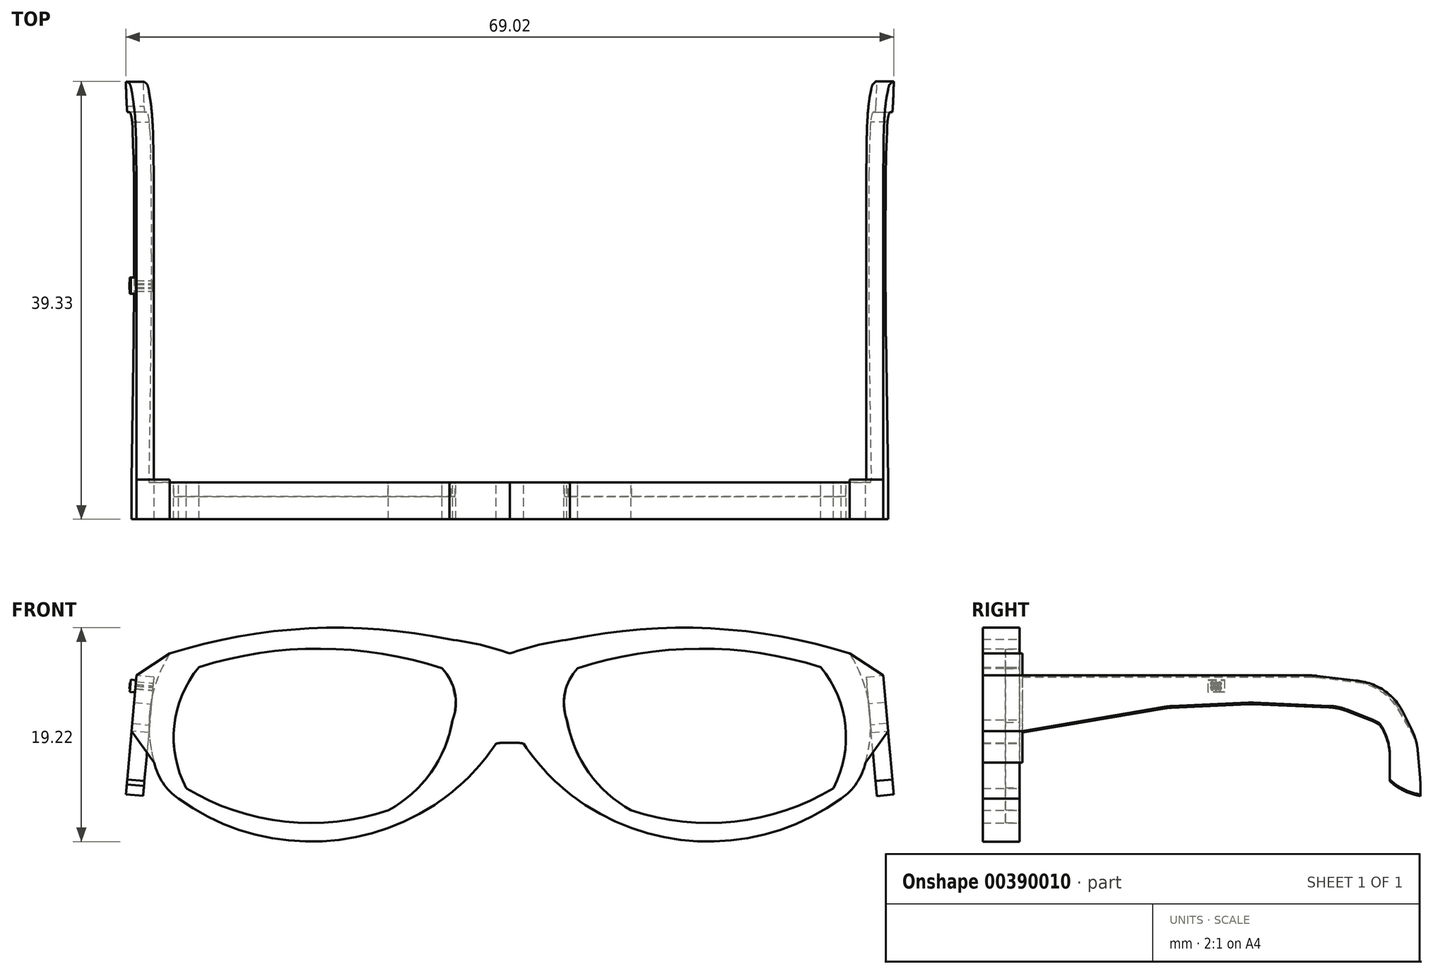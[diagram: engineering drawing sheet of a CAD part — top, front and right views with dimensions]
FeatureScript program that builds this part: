
annotation { "Feature Type Name" : "Feature", "Feature Type Description" : "" }
export const myFeature = defineFeature(function(context is Context, id is Id, definition is map)
    precondition{}
    {
        {
            var Q0;
            Q0=qCreatedBy(makeId("Front.planeOp"),FACE);
            var sketch = newSketch(context, id + "F0", { "sketchPlane" : qUnion([Q0])});
            skArc(sketch, "E0", {"start": v(27.94, 3.25) * mm, "mid": v(17.02, 4.8) * mm, "end": v(6.1, 3.16) * mm});
            skArc(sketch, "E1", {"start": v(29.08, -7.57) * mm, "mid": v(30, -2) * mm, "end": v(27.94, 3.25) * mm});
            skArc(sketch, "E2", {"start": v(10.95, -9.56) * mm, "mid": v(20.23, -10.57) * mm, "end": v(29.08, -7.57) * mm});
            skArc(sketch, "E3", {"start": v(5.25, -1.68) * mm, "mid": v(7.2, -6.28) * mm, "end": v(10.95, -9.56) * mm});
            skArc(sketch, "E4", {"start": v(6.1, 3.16) * mm, "mid": v(5.03, 0.85) * mm, "end": v(5.25, -1.68) * mm});
            skArc(sketch, "E5.MirrorCS", {"start": v(-27.94, 3.25) * mm, "mid": v(-17.02, 4.8) * mm, "end": v(-6.1, 3.16) * mm});
            skArc(sketch, "E6.MirrorCS", {"start": v(-6.1, 3.16) * mm, "mid": v(-5.03, 0.85) * mm, "end": v(-5.25, -1.68) * mm});
            skArc(sketch, "E7.MirrorCS", {"start": v(-5.25, -1.68) * mm, "mid": v(-7.2, -6.28) * mm, "end": v(-10.95, -9.56) * mm});
            skArc(sketch, "E8.MirrorCS", {"start": v(-10.95, -9.56) * mm, "mid": v(-20.23, -10.57) * mm, "end": v(-29.08, -7.57) * mm});
            skArc(sketch, "E9.MirrorCS", {"start": v(-29.08, -7.57) * mm, "mid": v(-30, -2) * mm, "end": v(-27.94, 3.25) * mm});
            skArc(sketch, "E10", {"start": v(10.95, -9.61) * mm, "mid": v(20.25, -10.67) * mm, "end": v(29.1, -7.6) * mm});
            skArc(sketch, "E11", {"start": v(5.15, -1.68) * mm, "mid": v(7.13, -6.32) * mm, "end": v(10.95, -9.61) * mm});
            skArc(sketch, "E12", {"start": v(6.1, 3.16) * mm, "mid": v(5, 0.85) * mm, "end": v(5.25, -1.68) * mm});
            skArc(sketch, "E13", {"start": v(27.94, 3.27) * mm, "mid": v(17, 4.88) * mm, "end": v(6.1, 3.16) * mm});
            skArc(sketch, "E14", {"start": v(29.08, -7.57) * mm, "mid": v(30.13, -1.98) * mm, "end": v(27.94, 3.27) * mm});
            skArc(sketch, "E15.MirrorCS", {"start": v(-5.15, -1.68) * mm, "mid": v(-7.13, -6.32) * mm, "end": v(-10.95, -9.61) * mm});
            skArc(sketch, "E16.MirrorCS", {"start": v(-10.95, -9.61) * mm, "mid": v(-20.25, -10.67) * mm, "end": v(-29.1, -7.6) * mm});
            skArc(sketch, "E17.MirrorCS", {"start": v(-29.08, -7.57) * mm, "mid": v(-30.13, -1.98) * mm, "end": v(-27.94, 3.27) * mm});
            skArc(sketch, "E18.MirrorCS", {"start": v(-27.94, 3.27) * mm, "mid": v(-17, 4.88) * mm, "end": v(-6.1, 3.16) * mm});
            skArc(sketch, "E19.MirrorCS", {"start": v(-6.1, 3.16) * mm, "mid": v(-5, 0.85) * mm, "end": v(-5.25, -1.68) * mm});
            skSolve(sketch);
        }
        {
            var Q0;
            Q0 = qSketchRegion(id + "F0", true);
            extrude(context, id + "F1", {"entities" : qUnion([Q0]), "depth" : 1.27 * mm});
        }
        {
            var Q0;
            Q0=qCreatedBy(makeId("Front.planeOp"),FACE);
            var sketch = newSketch(context, id + "F2", { "sketchPlane" : qUnion([Q0])});
            skArc(sketch, "E20", {"start": v(-6.09, 3.17) * mm, "mid": v(-17, 4.94) * mm, "end": v(-27.95, 3.27) * mm});
            skArc(sketch, "E21", {"start": v(-27.95, 3.27) * mm, "mid": v(-30.16, -2) * mm, "end": v(-29.08, -7.6) * mm});
            skArc(sketch, "E22", {"start": v(-29.08, -7.6) * mm, "mid": v(-20.21, -10.61) * mm, "end": v(-10.9, -9.6) * mm});
            skArc(sketch, "E23", {"start": v(-10.9, -9.6) * mm, "mid": v(-7.09, -6.19) * mm, "end": v(-5.13, -1.46) * mm});
            skArc(sketch, "E24", {"start": v(-5.13, -1.46) * mm, "mid": v(-4.95, 1) * mm, "end": v(-6.09, 3.17) * mm});
            skArc(sketch, "E25.MirrorCS", {"start": v(6.09, 3.17) * mm, "mid": v(17, 4.94) * mm, "end": v(27.95, 3.27) * mm});
            skArc(sketch, "E26.MirrorCS", {"start": v(5.13, -1.46) * mm, "mid": v(4.95, 1) * mm, "end": v(6.09, 3.17) * mm});
            skArc(sketch, "E27.MirrorCS", {"start": v(10.9, -9.6) * mm, "mid": v(7.09, -6.19) * mm, "end": v(5.13, -1.46) * mm});
            skArc(sketch, "E28.MirrorCS", {"start": v(29.08, -7.6) * mm, "mid": v(20.21, -10.61) * mm, "end": v(10.9, -9.6) * mm});
            skArc(sketch, "E29.MirrorCS", {"start": v(27.95, 3.27) * mm, "mid": v(30.16, -2) * mm, "end": v(29.08, -7.6) * mm});
            skSolve(sketch);
        }
        {
            var Q0;
            Q0=qCreatedBy(makeId("Front.planeOp"),FACE);
            var sketch = newSketch(context, id + "F3", { "sketchPlane" : qUnion([Q0])});
            skArc(sketch, "E30", {"start": v(0, -3.53) * mm, "mid": v(-0.62, -3.52) * mm, "end": v(-1.23, -3.59) * mm});
            skArc(sketch, "E31", {"start": v(-6.77, -9.12) * mm, "mid": v(-3.72, -6.63) * mm, "end": v(-1.23, -3.59) * mm});
            skArc(sketch, "E32", {"start": v(-29.78, -8.54) * mm, "mid": v(-18.37, -12.4) * mm, "end": v(-6.77, -9.12) * mm});
            skArc(sketch, "E33", {"start": v(-31.97, -5.28) * mm, "mid": v(-31.19, -7.12) * mm, "end": v(-29.78, -8.54) * mm});
            skArc(sketch, "E34", {"start": v(-30.56, 4.5) * mm, "mid": v(-32.3, -0.24) * mm, "end": v(-31.97, -5.28) * mm});
            skArc(sketch, "E35", {"start": v(-5.41, 5.77) * mm, "mid": v(-18.07, 6.76) * mm, "end": v(-30.56, 4.5) * mm});
            skArc(sketch, "E36", {"start": v(0, 4.5) * mm, "mid": v(-2.67, 5.3) * mm, "end": v(-5.41, 5.77) * mm});
            skArc(sketch, "E37.MirrorCS", {"start": v(0, 4.5) * mm, "mid": v(2.67, 5.3) * mm, "end": v(5.41, 5.77) * mm});
            skArc(sketch, "E38.MirrorCS", {"start": v(5.41, 5.77) * mm, "mid": v(18.07, 6.76) * mm, "end": v(30.56, 4.5) * mm});
            skArc(sketch, "E39.MirrorCS", {"start": v(30.56, 4.5) * mm, "mid": v(32.3, -0.24) * mm, "end": v(31.97, -5.28) * mm});
            skArc(sketch, "E40.MirrorCS", {"start": v(31.97, -5.28) * mm, "mid": v(31.19, -7.12) * mm, "end": v(29.78, -8.54) * mm});
            skArc(sketch, "E41.MirrorCS", {"start": v(29.78, -8.54) * mm, "mid": v(18.37, -12.4) * mm, "end": v(6.77, -9.12) * mm});
            skArc(sketch, "E42.MirrorCS", {"start": v(6.77, -9.12) * mm, "mid": v(3.72, -6.63) * mm, "end": v(1.23, -3.59) * mm});
            skArc(sketch, "E43.MirrorCS", {"start": v(0, -3.53) * mm, "mid": v(0.62, -3.52) * mm, "end": v(1.23, -3.59) * mm});
            skSolve(sketch);
        }
        {
            var Q0;
            Q0=makeQuery(id+"F3.imprint","IMPRINT",FACE,{"disambiguationData":[TD([[makeQuery(id+"F3.imprint","IMPRINT",EDGE,{"derivedFrom":sQuery(id+"F3.wireOp",EDGE,"E30")}),-1.0]])]});
            var Q1;
            Q1 = qSketchRegion(id + "F2", true);
            var Q2;
            Q2 = qSketchRegion(id + "F3", true);
            extrude(context, id + "F4", {"entities" : qUnion([Q0, Q1, Q2]), "depth" : 3.3 * mm});
        }
        {
            var Q0;
            Q0=makeQuery(id+"F4.opExtrude","CAP_FACE",FACE,{"disambiguationData":[OSD([sQuery(id+"F3.wireOp",EDGE,"E30"),sQuery(id+"F3.wireOp",EDGE,"E31"),sQuery(id+"F3.wireOp",EDGE,"E32"),sQuery(id+"F3.wireOp",EDGE,"E33"),sQuery(id+"F3.wireOp",EDGE,"E34"),sQuery(id+"F3.wireOp",EDGE,"E35"),sQuery(id+"F3.wireOp",EDGE,"E36"),sQuery(id+"F3.wireOp",EDGE,"E37.MirrorCS"),sQuery(id+"F3.wireOp",EDGE,"E38.MirrorCS"),sQuery(id+"F3.wireOp",EDGE,"E39.MirrorCS"),sQuery(id+"F3.wireOp",EDGE,"E40.MirrorCS"),sQuery(id+"F3.wireOp",EDGE,"E41.MirrorCS"),sQuery(id+"F3.wireOp",EDGE,"E42.MirrorCS"),sQuery(id+"F3.wireOp",EDGE,"E43.MirrorCS")])],"isStart":false});
            var sketch = newSketch(context, id + "F5", { "sketchPlane" : qUnion([Q0])});
            skLineSegment(sketch, "E44", {"start": v(30.56, 4.5) * mm, "end": v(33.55, 2.53) * mm});
            skLineSegment(sketch, "E45", {"start": v(33.55, 2.53) * mm, "end": v(34, -2.46) * mm});
            skLineSegment(sketch, "E46", {"start": v(34, -2.46) * mm, "end": v(31.97, -5.28) * mm});
            skLineSegment(sketch, "E47.MirrorCS", {"start": v(-34, -2.46) * mm, "end": v(-31.97, -5.28) * mm});
            skLineSegment(sketch, "E48.MirrorCS", {"start": v(-33.55, 2.53) * mm, "end": v(-34, -2.46) * mm});
            skLineSegment(sketch, "E49.MirrorCS", {"start": v(-30.56, 4.5) * mm, "end": v(-33.55, 2.53) * mm});
            skSolve(sketch);
        }
        {
            var Q0;
            Q0 = qSketchRegion(id + "F5", true);
            var Q1;
            Q1=makeQuery(id+"F5.imprint","IMPRINT",FACE,{"disambiguationData":[TD([[makeQuery(id+"F5.imprint","IMPRINT",EDGE,{"derivedFrom":sQuery(id+"F5.wireOp",EDGE,"E44")}),-1.0]])]});
            var Q2;
            Q2=makeQuery(id+"F5.imprint","IMPRINT",FACE,{"disambiguationData":[TD([[makeQuery(id+"F5.imprint","IMPRINT",EDGE,{"derivedFrom":sQuery(id+"F5.wireOp",EDGE,"E47.MirrorCS")}),1.0]])]});
            extrude(context, id + "F6", {"entities" : qUnion([Q0, Q1, Q2]), "operationType" : NewBodyOperationType.ADD, "oppositeDirection" : true, "depth" : 3.56 * mm});
        }
        {
            var Q0;
            Q0=makeQuery(id+"F6.opExtrude","SWEPT_FACE",FACE,{"disambiguationData":[OSD([sQuery(id+"F5.wireOp",EDGE,"E45")])]});
            var sketch = newSketch(context, id + "F7", { "sketchPlane" : qUnion([Q0])});
            skLineSegment(sketch, "E50", {"start": v(0.25, -0.48) * mm, "end": v(20.8, -0.48) * mm});
            skLineSegment(sketch, "E51", {"start": v(20.8, -0.48) * mm, "end": v(26.45, -0.48) * mm});
            skLineSegment(sketch, "E52", {"start": v(26.45, -0.48) * mm, "end": v(32.77, -1.26) * mm});
            skLineSegment(sketch, "E53", {"start": v(32.77, -1.26) * mm, "end": v(34.38, -3.55) * mm});
            skLineSegment(sketch, "E54", {"start": v(34.38, -3.55) * mm, "end": v(35.71, -6.31) * mm});
            skLineSegment(sketch, "E55", {"start": v(35.71, -6.31) * mm, "end": v(36.03, -9.94) * mm});
            skLineSegment(sketch, "E56", {"start": v(36.03, -9.94) * mm, "end": v(36.03, -11.22) * mm});
            skLineSegment(sketch, "E57", {"start": v(36.03, -11.22) * mm, "end": v(35.46, -11.5) * mm});
            skLineSegment(sketch, "E58", {"start": v(35.46, -11.5) * mm, "end": v(33.25, -9.9) * mm});
            skLineSegment(sketch, "E59", {"start": v(33.25, -9.9) * mm, "end": v(33.28, -9.86) * mm});
            skLineSegment(sketch, "E60", {"start": v(33.28, -9.86) * mm, "end": v(33.28, -5.53) * mm});
            skLineSegment(sketch, "E61", {"start": v(33.28, -5.53) * mm, "end": v(32.47, -4.74) * mm});
            skLineSegment(sketch, "E62", {"start": v(32.47, -4.74) * mm, "end": v(28.68, -3.26) * mm});
            skLineSegment(sketch, "E63", {"start": v(28.68, -3.26) * mm, "end": v(20.8, -2.92) * mm});
            skLineSegment(sketch, "E64", {"start": v(20.8, -2.92) * mm, "end": v(13.36, -3.26) * mm});
            skLineSegment(sketch, "E65", {"start": v(13.36, -3.26) * mm, "end": v(0.25, -5.49) * mm});
            skSolve(sketch);
        }
        {
            var Q0;
            Q0=makeQuery(id+"F6.opExtrude","SWEPT_FACE",FACE,{"disambiguationData":[OSD([sQuery(id+"F5.wireOp",EDGE,"E48.MirrorCS")])]});
            var sketch = newSketch(context, id + "F8", { "sketchPlane" : qUnion([Q0])});
            skLineSegment(sketch, "E66", {"start": v(-0.25, -0.48) * mm, "end": v(-26.44, -0.48) * mm});
            skLineSegment(sketch, "E67", {"start": v(-26.44, -0.48) * mm, "end": v(-32.74, -1.23) * mm});
            skLineSegment(sketch, "E68", {"start": v(-32.74, -1.23) * mm, "end": v(-35.71, -6.3) * mm});
            skLineSegment(sketch, "E69", {"start": v(-35.71, -6.3) * mm, "end": v(-36.03, -9.9) * mm});
            skLineSegment(sketch, "E70", {"start": v(-36.03, -9.9) * mm, "end": v(-36.03, -11.2) * mm});
            skLineSegment(sketch, "E71", {"start": v(-36.03, -11.2) * mm, "end": v(-35.45, -11.5) * mm});
            skLineSegment(sketch, "E72", {"start": v(-35.45, -11.5) * mm, "end": v(-33.25, -9.9) * mm});
            skLineSegment(sketch, "E73", {"start": v(-33.25, -9.9) * mm, "end": v(-33.28, -9.86) * mm});
            skLineSegment(sketch, "E74", {"start": v(-33.28, -9.86) * mm, "end": v(-33.28, -5.53) * mm});
            skLineSegment(sketch, "E75", {"start": v(-33.28, -5.53) * mm, "end": v(-32.47, -4.74) * mm});
            skLineSegment(sketch, "E76", {"start": v(-32.47, -4.74) * mm, "end": v(-28.68, -3.26) * mm});
            skLineSegment(sketch, "E77", {"start": v(-28.68, -3.26) * mm, "end": v(-20.8, -2.92) * mm});
            skLineSegment(sketch, "E78", {"start": v(-20.8, -2.92) * mm, "end": v(-13.36, -3.26) * mm});
            skLineSegment(sketch, "E79", {"start": v(-13.36, -3.26) * mm, "end": v(-0.25, -5.49) * mm});
            skSolve(sketch);
        }
        {
            var Q0;
            Q0=makeQuery(id+"F8.imprint","IMPRINT",FACE,{"disambiguationData":[TD([[makeQuery(id+"F8.imprint","IMPRINT",EDGE,{"derivedFrom":sQuery(id+"F8.wireOp",EDGE,"E66")}),1.0]])]});
            extrude(context, id + "F9", {"entities" : qUnion([Q0]), "operationType" : NewBodyOperationType.ADD, "oppositeDirection" : true, "depth" : 1.55 * mm});
        }
        {
            var Q0;
            Q0=makeQuery(id+"F7.imprint","IMPRINT",FACE,{"disambiguationData":[TD([[makeQuery(id+"F7.imprint","IMPRINT",EDGE,{"derivedFrom":sQuery(id+"F7.wireOp",EDGE,"E50")}),-1.0]])]});
            extrude(context, id + "F10", {"entities" : qUnion([Q0]), "operationType" : NewBodyOperationType.ADD, "oppositeDirection" : true, "depth" : 1.52 * mm});
        }
        {
            var Q0;
            Q0=makeQuery(id+"F9.opExtrude","SWEPT_EDGE",EDGE,{"disambiguationData":[OSD([sQuery(id+"F8.wireOp",EDGE,"E67"),sQuery(id+"F8.wireOp",EDGE,"E68")])]});
            var Q1;
            Q1=makeQuery(id+"F9.opExtrude","SWEPT_EDGE",EDGE,{"disambiguationData":[OSD([sQuery(id+"F8.wireOp",EDGE,"E66"),sQuery(id+"F8.wireOp",EDGE,"E67")])]});
            var Q2;
            Q2=makeQuery(id+"F9.opExtrude","SWEPT_EDGE",EDGE,{"disambiguationData":[OSD([sQuery(id+"F8.wireOp",EDGE,"E68"),sQuery(id+"F8.wireOp",EDGE,"E69")])]});
            var Q3;
            Q3=makeQuery(id+"F9.opExtrude","SWEPT_EDGE",EDGE,{"disambiguationData":[OSD([sQuery(id+"F8.wireOp",EDGE,"E71"),sQuery(id+"F8.wireOp",EDGE,"E72")])]});
            var Q4;
            Q4=makeQuery(id+"F9.opExtrude","SWEPT_EDGE",EDGE,{"disambiguationData":[OSD([sQuery(id+"F8.wireOp",EDGE,"E72"),sQuery(id+"F8.wireOp",EDGE,"E73")])]});
            var Q5;
            Q5=makeQuery(id+"F9.opExtrude","SWEPT_EDGE",EDGE,{"disambiguationData":[OSD([sQuery(id+"F8.wireOp",EDGE,"E74"),sQuery(id+"F8.wireOp",EDGE,"E75")])]});
            var Q6;
            Q6=makeQuery(id+"F9.opExtrude","SWEPT_EDGE",EDGE,{"disambiguationData":[OSD([sQuery(id+"F8.wireOp",EDGE,"E75"),sQuery(id+"F8.wireOp",EDGE,"E76")])]});
            var Q7;
            Q7=makeQuery(id+"F9.opExtrude","SWEPT_EDGE",EDGE,{"disambiguationData":[OSD([sQuery(id+"F8.wireOp",EDGE,"E76"),sQuery(id+"F8.wireOp",EDGE,"E77")])]});
            var Q8;
            Q8=makeQuery(id+"F9.opExtrude","SWEPT_EDGE",EDGE,{"disambiguationData":[OSD([sQuery(id+"F8.wireOp",EDGE,"E77"),sQuery(id+"F8.wireOp",EDGE,"E78")])]});
            var Q9;
            Q9=makeQuery(id+"F9.opExtrude","SWEPT_EDGE",EDGE,{"disambiguationData":[OSD([sQuery(id+"F8.wireOp",EDGE,"E78"),sQuery(id+"F8.wireOp",EDGE,"E79")])]});
            var Q10;
            Q10=makeQuery(id+"F10.opExtrude","SWEPT_EDGE",EDGE,{"disambiguationData":[OSD([sQuery(id+"F7.wireOp",EDGE,"E51"),sQuery(id+"F7.wireOp",EDGE,"E52")])]});
            var Q11;
            Q11=makeQuery(id+"F10.opExtrude","SWEPT_EDGE",EDGE,{"disambiguationData":[OSD([sQuery(id+"F7.wireOp",EDGE,"E52"),sQuery(id+"F7.wireOp",EDGE,"E53")])]});
            var Q12;
            Q12=makeQuery(id+"F10.opExtrude","SWEPT_EDGE",EDGE,{"disambiguationData":[OSD([sQuery(id+"F7.wireOp",EDGE,"E53"),sQuery(id+"F7.wireOp",EDGE,"E54")])]});
            var Q13;
            Q13=makeQuery(id+"F10.opExtrude","SWEPT_EDGE",EDGE,{"disambiguationData":[OSD([sQuery(id+"F7.wireOp",EDGE,"E54"),sQuery(id+"F7.wireOp",EDGE,"E55")])]});
            var Q14;
            Q14=makeQuery(id+"F10.opExtrude","SWEPT_EDGE",EDGE,{"disambiguationData":[OSD([sQuery(id+"F7.wireOp",EDGE,"E55"),sQuery(id+"F7.wireOp",EDGE,"E56")])]});
            var Q15;
            Q15=makeQuery(id+"F10.opExtrude","SWEPT_EDGE",EDGE,{"disambiguationData":[OSD([sQuery(id+"F7.wireOp",EDGE,"E57"),sQuery(id+"F7.wireOp",EDGE,"E58")])]});
            var Q16;
            Q16=makeQuery(id+"F10.opExtrude","SWEPT_EDGE",EDGE,{"disambiguationData":[OSD([sQuery(id+"F7.wireOp",EDGE,"E58"),sQuery(id+"F7.wireOp",EDGE,"E59")])]});
            var Q17;
            Q17=makeQuery(id+"F10.opExtrude","SWEPT_EDGE",EDGE,{"disambiguationData":[OSD([sQuery(id+"F7.wireOp",EDGE,"E60"),sQuery(id+"F7.wireOp",EDGE,"E61")])]});
            var Q18;
            Q18=makeQuery(id+"F10.opExtrude","SWEPT_EDGE",EDGE,{"disambiguationData":[OSD([sQuery(id+"F7.wireOp",EDGE,"E61"),sQuery(id+"F7.wireOp",EDGE,"E62")])]});
            var Q19;
            Q19=makeQuery(id+"F10.opExtrude","SWEPT_EDGE",EDGE,{"disambiguationData":[OSD([sQuery(id+"F7.wireOp",EDGE,"E62"),sQuery(id+"F7.wireOp",EDGE,"E63")])]});
            var Q20;
            Q20=makeQuery(id+"F10.opExtrude","SWEPT_EDGE",EDGE,{"disambiguationData":[OSD([sQuery(id+"F7.wireOp",EDGE,"E63"),sQuery(id+"F7.wireOp",EDGE,"E64")])]});
            var Q21;
            Q21=makeQuery(id+"F10.opExtrude","SWEPT_EDGE",EDGE,{"disambiguationData":[OSD([sQuery(id+"F7.wireOp",EDGE,"E64"),sQuery(id+"F7.wireOp",EDGE,"E65")])]});
            fillet(context, id + "F11", {"entities" : qUnion([Q0, Q1, Q2, Q3, Q4, Q5, Q6, Q7, Q8, Q9, Q10, Q11, Q12, Q13, Q14, Q15, Q16, Q17, Q18, Q19, Q20, Q21]), "radius" : 5.08 * mm, "tangentPropagation" : true, "allowEdgeOverflow" : false});
        }
        {
            var Q0;
            Q0=makeQuery(id+"F9.opExtrude","CAP_FACE",FACE,{"disambiguationData":[OSD([sQuery(id+"F5.wireOp",EDGE,"E48.MirrorCS"),sQuery(id+"F8.wireOp",EDGE,"E66"),sQuery(id+"F8.wireOp",EDGE,"E67"),sQuery(id+"F8.wireOp",EDGE,"E68"),sQuery(id+"F8.wireOp",EDGE,"E69"),sQuery(id+"F8.wireOp",EDGE,"E70"),sQuery(id+"F8.wireOp",EDGE,"E71"),sQuery(id+"F8.wireOp",EDGE,"E72"),sQuery(id+"F8.wireOp",EDGE,"E73"),sQuery(id+"F8.wireOp",EDGE,"E74"),sQuery(id+"F8.wireOp",EDGE,"E75"),sQuery(id+"F8.wireOp",EDGE,"E76"),sQuery(id+"F8.wireOp",EDGE,"E77"),sQuery(id+"F8.wireOp",EDGE,"E78"),sQuery(id+"F8.wireOp",EDGE,"E79")])],"isStart":false});
            var sketch = newSketch(context, id + "F12", { "sketchPlane" : qUnion([Q0])});
            skCircle(sketch, "E80", {"center": v(17.32, -1.16) * mm, "radius": 0.1 * mm});
            skCircle(sketch, "E81", {"center": v(17.32, -1.54) * mm, "radius": 0.1 * mm});
            skCircle(sketch, "E82", {"center": v(17.67, -1.57) * mm, "radius": 0.1 * mm});
            skCircle(sketch, "E83", {"center": v(17.67, -1.17) * mm, "radius": 0.1 * mm});
            skCircle(sketch, "E84", {"center": v(18, -1.57) * mm, "radius": 0.1 * mm});
            skCircle(sketch, "E85", {"center": v(18, -1.17) * mm, "radius": 0.1 * mm});
            skSolve(sketch);
        }
        {
            var Q0;
            Q0=sQuery(id+"F12.wireOp",VERTEX,"E83.center");
            var Q1;
            Q1=sQuery(id+"F12.wireOp",VERTEX,"E80.center");
            var Q2;
            Q2=sQuery(id+"F12.wireOp",VERTEX,"E85.center");
            var Q3;
            Q3=sQuery(id+"F12.wireOp",VERTEX,"E84.center");
            var Q4;
            Q4=sQuery(id+"F12.wireOp",VERTEX,"E82.center");
            var Q5;
            Q5=sQuery(id+"F12.wireOp",VERTEX,"E81.center");
            var Q6;
            Q6=makeQuery(id+"F4.opExtrude","SWEPT_BODY",BODY,{"disambiguationData":[OSD([sQuery(id+"F3.wireOp",EDGE,"E30"),sQuery(id+"F3.wireOp",EDGE,"E31"),sQuery(id+"F3.wireOp",EDGE,"E32"),sQuery(id+"F3.wireOp",EDGE,"E33"),sQuery(id+"F3.wireOp",EDGE,"E34"),sQuery(id+"F3.wireOp",EDGE,"E35"),sQuery(id+"F3.wireOp",EDGE,"E36"),sQuery(id+"F3.wireOp",EDGE,"E37.MirrorCS"),sQuery(id+"F3.wireOp",EDGE,"E38.MirrorCS"),sQuery(id+"F3.wireOp",EDGE,"E39.MirrorCS"),sQuery(id+"F3.wireOp",EDGE,"E40.MirrorCS"),sQuery(id+"F3.wireOp",EDGE,"E41.MirrorCS"),sQuery(id+"F3.wireOp",EDGE,"E42.MirrorCS"),sQuery(id+"F3.wireOp",EDGE,"E43.MirrorCS")])]});
            hole(context, id + "F13", {"style" : HoleStyle.SIMPLE, "endStyle" : HoleEndStyle.THROUGH, "holeDiameter" : 0.25 * mm, "isTappedThrough" : true, "tappedDepth" : 12.7 * mm, "tapClearance" : 3, "locations" : qUnion([Q0, Q1, Q2, Q3, Q4, Q5]), "scope" : qUnion([Q6])});
        }
        {
            var Q0;
            {var subQ0=sQuery(id+"F5.wireOp",EDGE,"E48.MirrorCS");Q0=makeQuery(id+"F9.boolean.opBoolean","MERGE",FACE,{"derivedFrom":[makeQuery(id+"F6.opExtrude","SWEPT_FACE",FACE,{"disambiguationData":[OSD([subQ0])]}),makeQuery(id+"F9.opExtrude","CAP_FACE",FACE,{"disambiguationData":[OSD([subQ0,sQuery(id+"F8.wireOp",EDGE,"E66"),sQuery(id+"F8.wireOp",EDGE,"E67"),sQuery(id+"F8.wireOp",EDGE,"E68"),sQuery(id+"F8.wireOp",EDGE,"E69"),sQuery(id+"F8.wireOp",EDGE,"E70"),sQuery(id+"F8.wireOp",EDGE,"E71"),sQuery(id+"F8.wireOp",EDGE,"E72"),sQuery(id+"F8.wireOp",EDGE,"E73"),sQuery(id+"F8.wireOp",EDGE,"E74"),sQuery(id+"F8.wireOp",EDGE,"E75"),sQuery(id+"F8.wireOp",EDGE,"E76"),sQuery(id+"F8.wireOp",EDGE,"E77"),sQuery(id+"F8.wireOp",EDGE,"E78"),sQuery(id+"F8.wireOp",EDGE,"E79")])],"isStart":true})]});}
            var sketch = newSketch(context, id + "F14", { "sketchPlane" : qUnion([Q0])});
            skLineSegment(sketch, "E86", {"start": v(-18.15, -2) * mm, "end": v(-16.97, -2) * mm});
            skLineSegment(sketch, "E87", {"start": v(-16.97, -2) * mm, "end": v(-16.97, -0.9) * mm});
            skLineSegment(sketch, "E88", {"start": v(-16.97, -0.9) * mm, "end": v(-18.42, -0.9) * mm});
            skLineSegment(sketch, "E89", {"start": v(-18.42, -0.9) * mm, "end": v(-18.42, -2) * mm});
            skLineSegment(sketch, "E90", {"start": v(-18.42, -2) * mm, "end": v(-18.15, -2) * mm});
            skSolve(sketch);
        }
        {
            var Q0;
            Q0 = qSketchRegion(id + "F14", true);
            extrude(context, id + "F15", {"entities" : qUnion([Q0]), "operationType" : NewBodyOperationType.ADD, "depth" : 0.48 * mm});
        }
        {
            var Q0;
            Q0=makeQuery(id+"F15.opExtrude","CAP_FACE",FACE,{"disambiguationData":[OSD([sQuery(id+"F14.wireOp",EDGE,"E86"),sQuery(id+"F14.wireOp",EDGE,"E87"),sQuery(id+"F14.wireOp",EDGE,"E88"),sQuery(id+"F14.wireOp",EDGE,"E89"),sQuery(id+"F14.wireOp",EDGE,"E90")])],"isStart":false});
            var sketch = newSketch(context, id + "F16", { "sketchPlane" : qUnion([Q0])});
            skLineSegment(sketch, "E91", {"start": v(-17.79, -1.22) * mm, "end": v(-17.76, -1.18) * mm});
            skLineSegment(sketch, "E92", {"start": v(-17.76, -1.18) * mm, "end": v(-17.68, -1.18) * mm});
            skLineSegment(sketch, "E93", {"start": v(-17.68, -1.18) * mm, "end": v(-17.63, -1.22) * mm});
            skLineSegment(sketch, "E94", {"start": v(-17.63, -1.22) * mm, "end": v(-17.6, -1.34) * mm});
            skLineSegment(sketch, "E95", {"start": v(-17.6, -1.34) * mm, "end": v(-17.33, -1.73) * mm});
            skLineSegment(sketch, "E96", {"start": v(-17.33, -1.73) * mm, "end": v(-18, -1.73) * mm});
            skLineSegment(sketch, "E97", {"start": v(-18, -1.73) * mm, "end": v(-17.8, -1.35) * mm});
            skLineSegment(sketch, "E98", {"start": v(-17.8, -1.35) * mm, "end": v(-17.79, -1.22) * mm});
            skSolve(sketch);
        }
        {
            var Q0;
            Q0 = qSketchRegion(id + "F16", true);
            extrude(context, id + "F17", {"entities" : qUnion([Q0]), "operationType" : NewBodyOperationType.ADD, "depth" : 0.05 * mm});
        }
    });
